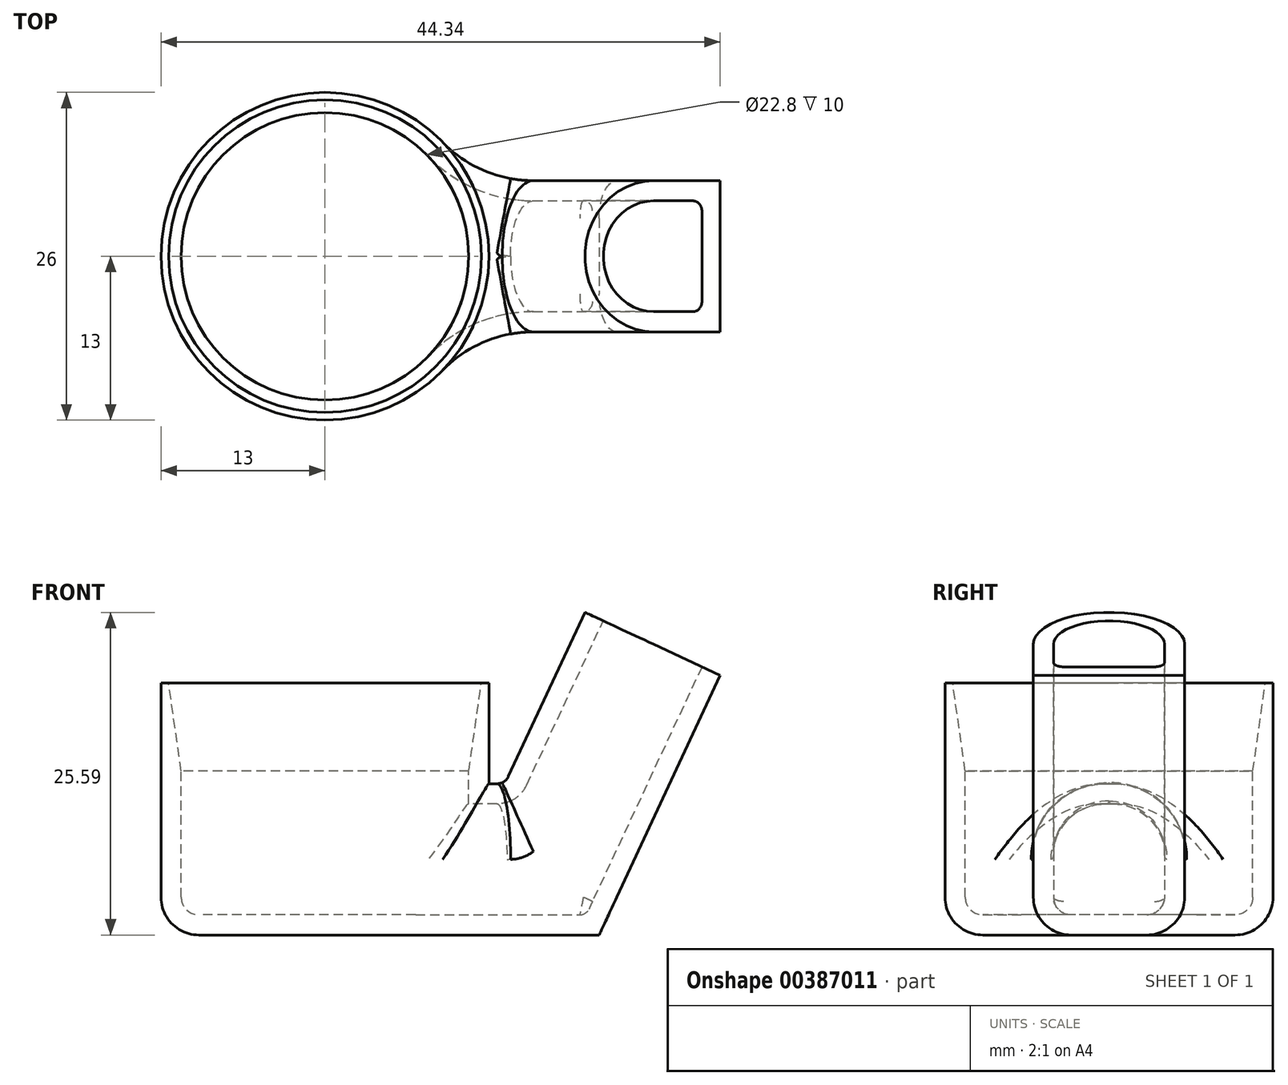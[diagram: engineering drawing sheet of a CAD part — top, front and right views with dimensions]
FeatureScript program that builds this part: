
annotation { "Feature Type Name" : "Feature", "Feature Type Description" : "" }
export const myFeature = defineFeature(function(context is Context, id is Id, definition is map)
    precondition{}
    {
        {
            var Q0;
            Q0=qCreatedBy(makeId("Top.planeOp"),FACE);
            var sketch = newSketch(context, id + "F0", { "sketchPlane" : qUnion([Q0])});
            skLineSegment(sketch, "E0.bottom", {"start": v(13, -13) * mm, "end": v(-13, -13) * mm});
            skLineSegment(sketch, "E0.top", {"start": v(13, 13) * mm, "end": v(-13, 13) * mm});
            skLineSegment(sketch, "E0.left", {"start": v(13, -13) * mm, "end": v(13, 13) * mm});
            skLineSegment(sketch, "E0.right", {"start": v(-13, -13) * mm, "end": v(-13, 13) * mm});
            skPoint(sketch, "E0.middle", {"position": v(0, 0) * mm});
            skSolve(sketch);
        }
        {
            var Q0;
            Q0 = qSketchRegion(id + "F0", true);
            extrude(context, id + "F1", {"entities" : qUnion([Q0]), "depth" : 20 * mm});
        }
        {
            var Q0;
            Q0=makeQuery(id+"F1.opExtrude","SWEPT_FACE",FACE,{"disambiguationData":[OSD([sQuery(id+"F0.wireOp",EDGE,"E0.left")])]});
            var sketch = newSketch(context, id + "F2", { "sketchPlane" : qUnion([Q0])});
            skLineSegment(sketch, "E1.bottom", {"start": v(6, 0) * mm, "end": v(-6, 0) * mm});
            skLineSegment(sketch, "E1.top", {"start": v(6, 12) * mm, "end": v(-6, 12) * mm});
            skLineSegment(sketch, "E1.left", {"start": v(6, 0) * mm, "end": v(6, 12) * mm});
            skLineSegment(sketch, "E1.right", {"start": v(-6, 0) * mm, "end": v(-6, 12) * mm});
            skSolve(sketch);
        }
        {
            var Q0;
            Q0 = qSketchRegion(id + "F2", true);
            extrude(context, id + "F3", {"entities" : qUnion([Q0]), "operationType" : NewBodyOperationType.ADD, "depth" : 12 * mm});
        }
        {
            var Q0;
            Q0=makeQuery(id+"F3.opExtrude","CAP_EDGE",EDGE,{"disambiguationData":[OSD([sQuery(id+"F2.wireOp",EDGE,"E1.top")])],"isStart":false});
            chamfer(context, id + "F4", {"entities" : qUnion([Q0]), "chamferType" : ChamferType.OFFSET_ANGLE, "width" : 5 * mm, "oppositeDirection" : false, "angle" : 65 * degree, "tangentPropagation" : true});
        }
        {
            var Q0;
            Q0=makeQuery(id+"F4.opChamfer","BLEND_FACE",FACE,{"disambiguationData":[OSD([sQuery(id+"F2.wireOp",EDGE,"E1.top")])]});
            extrude(context, id + "F5", {"entities" : qUnion([Q0]), "operationType" : NewBodyOperationType.ADD, "depth" : 15 * mm});
        }
        {
            var Q0;
            Q0=makeQuery(id+"F1.opExtrude","SWEPT_EDGE",EDGE,{"disambiguationData":[OSD([sQuery(id+"F0.wireOp",EDGE,"E0.top"),sQuery(id+"F0.wireOp",EDGE,"E0.right")])]});
            var Q1;
            Q1=makeQuery(id+"F1.opExtrude","SWEPT_EDGE",EDGE,{"disambiguationData":[OSD([sQuery(id+"F0.wireOp",EDGE,"E0.bottom"),sQuery(id+"F0.wireOp",EDGE,"E0.right")])]});
            var Q2;
            Q2=makeQuery(id+"F1.opExtrude","SWEPT_EDGE",EDGE,{"disambiguationData":[OSD([sQuery(id+"F0.wireOp",EDGE,"E0.top"),sQuery(id+"F0.wireOp",EDGE,"E0.left")])]});
            var Q3;
            Q3=makeQuery(id+"F1.opExtrude","SWEPT_EDGE",EDGE,{"disambiguationData":[OSD([sQuery(id+"F0.wireOp",EDGE,"E0.bottom"),sQuery(id+"F0.wireOp",EDGE,"E0.left")])]});
            fillet(context, id + "F6", {"entities" : qUnion([Q0, Q1, Q2, Q3]), "radius" : 13 * mm, "tangentPropagation" : true, "allowEdgeOverflow" : false});
        }
        {
            var Q0;
            Q0=makeQuery(id+"F5.opExtrude","SWEPT_FACE",FACE,{"disambiguationData":[OSD([sQuery(id+"F2.wireOp",EDGE,"E1.bottom"),sQuery(id+"F2.wireOp",EDGE,"E1.top"),sQuery(id+"F2.wireOp",EDGE,"E1.left"),sQuery(id+"F2.wireOp",EDGE,"E1.right")])]});
            var sketch = newSketch(context, id + "F7", { "sketchPlane" : qUnion([Q0])});
            skLineSegment(sketch, "E2.bottom", {"start": v(-6, 16.9) * mm, "end": v(6, 16.9) * mm});
            skLineSegment(sketch, "E2.top", {"start": v(-6, 20.23) * mm, "end": v(6, 20.23) * mm});
            skLineSegment(sketch, "E2.left", {"start": v(-6, 16.9) * mm, "end": v(-6, 20.23) * mm});
            skLineSegment(sketch, "E2.right", {"start": v(6, 16.9) * mm, "end": v(6, 20.23) * mm});
            skSolve(sketch);
        }
        {
            var Q0;
            Q0 = qSketchRegion(id + "F7", true);
            extrude(context, id + "F8", {"entities" : qUnion([Q0]), "operationType" : NewBodyOperationType.ADD, "depth" : 25 * mm, "offsetDistance" : 25 * mm});
        }
        {
            var Q0;
            Q0=makeQuery(id+"F8.opExtrude","SWEPT_FACE",FACE,{"disambiguationData":[OSD([sQuery(id+"F7.wireOp",EDGE,"E2.bottom")])]});
            extrude(context, id + "F9", {"entities" : qUnion([Q0]), "operationType" : NewBodyOperationType.REMOVE, "depth" : 25 * mm, "offsetDistance" : 25 * mm});
        }
        {
            var Q0;
            Q0=makeQuery(id+"F8.opExtrude","SWEPT_FACE",FACE,{"disambiguationData":[OSD([sQuery(id+"F7.wireOp",EDGE,"E2.bottom")])]});
            extrude(context, id + "F10", {"entities" : qUnion([Q0]), "operationType" : NewBodyOperationType.REMOVE, "oppositeDirection" : true, "depth" : 25 * mm, "offsetDistance" : 25 * mm});
        }
        {
            var Q0;
            {var subQ0=sQuery(id+"F2.wireOp",EDGE,"E1.right");Q0=makeQuery(id+"F6.opFillet","BLEND_EDGE",EDGE,{"blendedFrom":[makeQuery(id+"F1.opExtrude","SWEPT_EDGE",EDGE,{"disambiguationData":[OSD([sQuery(id+"F0.wireOp",EDGE,"E0.bottom"),sQuery(id+"F0.wireOp",EDGE,"E0.left")])]}),makeQuery(id+"F5.boolean.opBoolean","MERGE",FACE,{"derivedFrom":[makeQuery(id+"F3.opExtrude","SWEPT_FACE",FACE,{"disambiguationData":[OSD([subQ0])]}),makeQuery(id+"F5.opExtrude","SWEPT_FACE",FACE,{"disambiguationData":[OSD([sQuery(id+"F2.wireOp",EDGE,"E1.top"),subQ0])]})]})],"blendedInto":[makeQuery(id+"F5.boolean.opBoolean","MERGE",FACE,{"derivedFrom":[makeQuery(id+"F3.opExtrude","SWEPT_FACE",FACE,{"disambiguationData":[OSD([subQ0])]}),makeQuery(id+"F5.opExtrude","SWEPT_FACE",FACE,{"disambiguationData":[OSD([sQuery(id+"F2.wireOp",EDGE,"E1.top"),subQ0])]})]})]});}
            var Q1;
            {var subQ0=sQuery(id+"F2.wireOp",EDGE,"E1.left");Q1=makeQuery(id+"F6.opFillet","BLEND_EDGE",EDGE,{"blendedFrom":[makeQuery(id+"F1.opExtrude","SWEPT_EDGE",EDGE,{"disambiguationData":[OSD([sQuery(id+"F0.wireOp",EDGE,"E0.top"),sQuery(id+"F0.wireOp",EDGE,"E0.left")])]}),makeQuery(id+"F5.boolean.opBoolean","MERGE",FACE,{"derivedFrom":[makeQuery(id+"F3.opExtrude","SWEPT_FACE",FACE,{"disambiguationData":[OSD([subQ0])]}),makeQuery(id+"F5.opExtrude","SWEPT_FACE",FACE,{"disambiguationData":[OSD([sQuery(id+"F2.wireOp",EDGE,"E1.top"),subQ0])]})]})],"blendedInto":[makeQuery(id+"F5.boolean.opBoolean","MERGE",FACE,{"derivedFrom":[makeQuery(id+"F3.opExtrude","SWEPT_FACE",FACE,{"disambiguationData":[OSD([subQ0])]}),makeQuery(id+"F5.opExtrude","SWEPT_FACE",FACE,{"disambiguationData":[OSD([sQuery(id+"F2.wireOp",EDGE,"E1.top"),subQ0])]})]})]});}
            fillet(context, id + "F11", {"entities" : qUnion([Q0, Q1]), "radius" : 10 * mm, "tangentPropagation" : true, "allowEdgeOverflow" : false});
        }
        {
            var Q0;
            Q0=makeQuery(id+"F6.opFillet","BLEND_EDGE",EDGE,{"blendedFrom":[makeQuery(id+"F1.opExtrude","SWEPT_EDGE",EDGE,{"disambiguationData":[OSD([sQuery(id+"F0.wireOp",EDGE,"E0.top"),sQuery(id+"F0.wireOp",EDGE,"E0.left")])]}),makeQuery(id+"F3.opExtrude","SWEPT_FACE",FACE,{"disambiguationData":[OSD([sQuery(id+"F2.wireOp",EDGE,"E1.top")])]})],"blendedInto":[makeQuery(id+"F3.opExtrude","SWEPT_FACE",FACE,{"disambiguationData":[OSD([sQuery(id+"F2.wireOp",EDGE,"E1.top")])]})]});
            var Q1;
            {var subQ0=sQuery(id+"F2.wireOp",EDGE,"E1.top");Q1=makeQuery(id+"F5.boolean.opBoolean","MERGE",EDGE,{"derivedFrom":[makeQuery(id+"F4.opChamfer","BLEND_EDGE",EDGE,{"blendedFrom":[makeQuery(id+"F3.opExtrude","CAP_EDGE",EDGE,{"disambiguationData":[OSD([subQ0])],"isStart":false}),makeQuery(id+"F3.opExtrude","SWEPT_FACE",FACE,{"disambiguationData":[OSD([subQ0])]})],"blendedInto":[makeQuery(id+"F3.opExtrude","SWEPT_FACE",FACE,{"disambiguationData":[OSD([subQ0])]})]}),makeQuery(id+"F5.opExtrude","CAP_EDGE",EDGE,{"disambiguationData":[OSD([subQ0])],"isStart":true})]});}
            fillet(context, id + "F12", {"entities" : qUnion([Q0, Q1]), "radius" : 1 * mm, "tangentPropagation" : true, "allowEdgeOverflow" : false});
        }
        {
            var Q0;
            Q0=makeQuery(id+"F5.opExtrude","SWEPT_EDGE",EDGE,{"disambiguationData":[OSD([sQuery(id+"F2.wireOp",EDGE,"E1.top"),sQuery(id+"F2.wireOp",EDGE,"E1.left")])]});
            var Q1;
            {var subQ0=sQuery(id+"F7.wireOp",EDGE,"E2.right");var subQ1=sQuery(id+"F7.wireOp",EDGE,"E2.bottom");var subQ2=sQuery(id+"F2.wireOp",EDGE,"E1.right");var subQ3=sQuery(id+"F2.wireOp",EDGE,"E1.left");var subQ4=sQuery(id+"F2.wireOp",EDGE,"E1.top");var subQ5=sQuery(id+"F2.wireOp",EDGE,"E1.bottom");Q1=makeQuery(id+"F10.boolean.opBoolean","MERGE",EDGE,{"derivedFrom":[makeQuery(id+"F5.opExtrude","SWEPT_EDGE",EDGE,{"disambiguationData":[OSD([subQ5,subQ4,subQ3,subQ2]),TDD([makeQuery(id+"F4.opChamfer","BLEND_VERTEX",VERTEX,{"blendedFrom":[makeQuery(id+"F3.opExtrude","CAP_EDGE",EDGE,{"disambiguationData":[OSD([subQ4])],"isStart":false}),makeQuery(id+"F3.opExtrude","CAP_FACE",FACE,{"disambiguationData":[OSD([subQ5,subQ4,subQ3,subQ2])],"isStart":false}),makeQuery(id+"F3.opExtrude","SWEPT_FACE",FACE,{"disambiguationData":[OSD([subQ3])]})],"blendedInto":[makeQuery(id+"F3.opExtrude","CAP_FACE",FACE,{"disambiguationData":[OSD([subQ5,subQ4,subQ3,subQ2])],"isStart":false}),makeQuery(id+"F3.opExtrude","SWEPT_FACE",FACE,{"disambiguationData":[OSD([subQ3])]})]})])]}),makeQuery(id+"F9.boolean.opBoolean","COPY",EDGE,{"derivedFrom":makeQuery(id+"F9.opExtrude","SWEPT_EDGE",EDGE,{"disambiguationData":[OSD([subQ5,subQ4,subQ3,subQ2,subQ1,subQ0])]})}),makeQuery(id+"F10.opExtrude","SWEPT_EDGE",EDGE,{"disambiguationData":[OSD([subQ5,subQ4,subQ3,subQ2,subQ1,subQ0])]})]});}
            var Q2;
            Q2=makeQuery(id+"F5.opExtrude","SWEPT_EDGE",EDGE,{"disambiguationData":[OSD([sQuery(id+"F2.wireOp",EDGE,"E1.top"),sQuery(id+"F2.wireOp",EDGE,"E1.right")])]});
            var Q3;
            {var subQ0=sQuery(id+"F7.wireOp",EDGE,"E2.left");var subQ1=sQuery(id+"F7.wireOp",EDGE,"E2.bottom");var subQ2=sQuery(id+"F2.wireOp",EDGE,"E1.right");var subQ3=sQuery(id+"F2.wireOp",EDGE,"E1.left");var subQ4=sQuery(id+"F2.wireOp",EDGE,"E1.top");var subQ5=sQuery(id+"F2.wireOp",EDGE,"E1.bottom");Q3=makeQuery(id+"F10.boolean.opBoolean","MERGE",EDGE,{"derivedFrom":[makeQuery(id+"F5.opExtrude","SWEPT_EDGE",EDGE,{"disambiguationData":[OSD([subQ5,subQ4,subQ3,subQ2]),TDD([makeQuery(id+"F4.opChamfer","BLEND_VERTEX",VERTEX,{"blendedFrom":[makeQuery(id+"F3.opExtrude","CAP_EDGE",EDGE,{"disambiguationData":[OSD([subQ4])],"isStart":false}),makeQuery(id+"F3.opExtrude","CAP_FACE",FACE,{"disambiguationData":[OSD([subQ5,subQ4,subQ3,subQ2])],"isStart":false}),makeQuery(id+"F3.opExtrude","SWEPT_FACE",FACE,{"disambiguationData":[OSD([subQ2])]})],"blendedInto":[makeQuery(id+"F3.opExtrude","CAP_FACE",FACE,{"disambiguationData":[OSD([subQ5,subQ4,subQ3,subQ2])],"isStart":false}),makeQuery(id+"F3.opExtrude","SWEPT_FACE",FACE,{"disambiguationData":[OSD([subQ2])]})]})])]}),makeQuery(id+"F9.boolean.opBoolean","COPY",EDGE,{"derivedFrom":makeQuery(id+"F9.opExtrude","SWEPT_EDGE",EDGE,{"disambiguationData":[OSD([subQ5,subQ4,subQ3,subQ2,subQ1,subQ0])]})}),makeQuery(id+"F10.opExtrude","SWEPT_EDGE",EDGE,{"disambiguationData":[OSD([subQ5,subQ4,subQ3,subQ2,subQ1,subQ0])]})]});}
            fillet(context, id + "F13", {"entities" : qUnion([Q0, Q1, Q2, Q3]), "radius" : 6 * mm, "tangentPropagation" : true, "allowEdgeOverflow" : false});
        }
        {
            var Q0;
            {var subQ0=sQuery(id+"F0.wireOp",EDGE,"E0.left");var subQ1=sQuery(id+"F0.wireOp",EDGE,"E0.bottom");Q0=makeQuery(id+"F6.opFillet","BLEND_EDGE",EDGE,{"blendedFrom":[makeQuery(id+"F1.opExtrude","SWEPT_EDGE",EDGE,{"disambiguationData":[OSD([subQ1,subQ0])]}),makeQuery(id+"F3.boolean.opBoolean","MERGE",FACE,{"derivedFrom":[makeQuery(id+"F1.opExtrude","CAP_FACE",FACE,{"disambiguationData":[OSD([subQ1,sQuery(id+"F0.wireOp",EDGE,"E0.top"),subQ0,sQuery(id+"F0.wireOp",EDGE,"E0.right")])],"isStart":true}),makeQuery(id+"F3.opExtrude","SWEPT_FACE",FACE,{"disambiguationData":[OSD([sQuery(id+"F2.wireOp",EDGE,"E1.bottom")])]})]})],"blendedInto":[makeQuery(id+"F3.boolean.opBoolean","MERGE",FACE,{"derivedFrom":[makeQuery(id+"F1.opExtrude","CAP_FACE",FACE,{"disambiguationData":[OSD([subQ1,sQuery(id+"F0.wireOp",EDGE,"E0.top"),subQ0,sQuery(id+"F0.wireOp",EDGE,"E0.right")])],"isStart":true}),makeQuery(id+"F3.opExtrude","SWEPT_FACE",FACE,{"disambiguationData":[OSD([sQuery(id+"F2.wireOp",EDGE,"E1.bottom")])]})]})]});}
            fillet(context, id + "F14", {"entities" : qUnion([Q0]), "radius" : 3 * mm, "tangentPropagation" : true, "allowEdgeOverflow" : false});
        }
        {
            var Q0;
            Q0=makeQuery(id+"F1.opExtrude","CAP_FACE",FACE,{"disambiguationData":[OSD([sQuery(id+"F0.wireOp",EDGE,"E0.bottom"),sQuery(id+"F0.wireOp",EDGE,"E0.top"),sQuery(id+"F0.wireOp",EDGE,"E0.left"),sQuery(id+"F0.wireOp",EDGE,"E0.right")])],"isStart":false});
            var Q1;
            Q1=makeQuery(id+"F5.opExtrude","CAP_FACE",FACE,{"disambiguationData":[OSD([sQuery(id+"F2.wireOp",EDGE,"E1.top")])],"isStart":false});
            shell(context, id + "F15", {"entities" : qUnion([Q0, Q1]), "thickness" : 1.6 * mm});
        }
        {
            var Q0;
            {var subQ0=sQuery(id+"F2.wireOp",EDGE,"E1.top");var subQ1=sQuery(id+"F7.wireOp",EDGE,"E2.right");var subQ2=sQuery(id+"F7.wireOp",EDGE,"E2.bottom");var subQ3=sQuery(id+"F2.wireOp",EDGE,"E1.right");var subQ4=sQuery(id+"F2.wireOp",EDGE,"E1.left");var subQ5=sQuery(id+"F2.wireOp",EDGE,"E1.bottom");Q0=makeQuery(id+"F15.opShell","OFFSET_EDGE",EDGE,{"disambiguationData":[OSD([subQ5,subQ0,subQ4,subQ3,subQ2,subQ1]),TDD([makeQuery(id+"F13.opFillet","BLEND_EDGE",EDGE,{"blendedFrom":[makeQuery(id+"F10.boolean.opBoolean","MERGE",EDGE,{"derivedFrom":[makeQuery(id+"F5.opExtrude","SWEPT_EDGE",EDGE,{"disambiguationData":[OSD([subQ5,subQ0,subQ4,subQ3]),TDD([makeQuery(id+"F4.opChamfer","BLEND_VERTEX",VERTEX,{"blendedFrom":[makeQuery(id+"F3.opExtrude","CAP_EDGE",EDGE,{"disambiguationData":[OSD([subQ0])],"isStart":false}),makeQuery(id+"F3.opExtrude","CAP_FACE",FACE,{"disambiguationData":[OSD([subQ5,subQ0,subQ4,subQ3])],"isStart":false}),makeQuery(id+"F3.opExtrude","SWEPT_FACE",FACE,{"disambiguationData":[OSD([subQ4])]})],"blendedInto":[makeQuery(id+"F3.opExtrude","CAP_FACE",FACE,{"disambiguationData":[OSD([subQ5,subQ0,subQ4,subQ3])],"isStart":false}),makeQuery(id+"F3.opExtrude","SWEPT_FACE",FACE,{"disambiguationData":[OSD([subQ4])]})]})])]}),makeQuery(id+"F9.boolean.opBoolean","COPY",EDGE,{"derivedFrom":makeQuery(id+"F9.opExtrude","SWEPT_EDGE",EDGE,{"disambiguationData":[OSD([subQ5,subQ0,subQ4,subQ3,subQ2,subQ1])]})}),makeQuery(id+"F10.opExtrude","SWEPT_EDGE",EDGE,{"disambiguationData":[OSD([subQ5,subQ0,subQ4,subQ3,subQ2,subQ1])]})]}),makeQuery(id+"F5.opExtrude","CAP_FACE",FACE,{"disambiguationData":[OSD([subQ0])],"isStart":false})],"blendedInto":[makeQuery(id+"F5.opExtrude","CAP_FACE",FACE,{"disambiguationData":[OSD([subQ0])],"isStart":false})]})])]});}
            var Q1;
            {var subQ0=sQuery(id+"F2.wireOp",EDGE,"E1.top");Q1=makeQuery(id+"F13.opFillet","BLEND_EDGE",EDGE,{"blendedFrom":[makeQuery(id+"F5.opExtrude","SWEPT_EDGE",EDGE,{"disambiguationData":[OSD([subQ0,sQuery(id+"F2.wireOp",EDGE,"E1.right")])]}),makeQuery(id+"F5.opExtrude","CAP_FACE",FACE,{"disambiguationData":[OSD([subQ0])],"isStart":false})],"blendedInto":[makeQuery(id+"F5.opExtrude","CAP_FACE",FACE,{"disambiguationData":[OSD([subQ0])],"isStart":false})]});}
            fillet(context, id + "F16", {"entities" : qUnion([Q0, Q1]), "radius" : 0.8 * mm, "tangentPropagation" : true, "allowEdgeOverflow" : false});
        }
        {
            var Q0;
            Q0=makeQuery(id+"F15.opShell","OFFSET_EDGE",EDGE,{"disambiguationData":[OSD([sQuery(id+"F0.wireOp",EDGE,"E0.bottom"),sQuery(id+"F0.wireOp",EDGE,"E0.top"),sQuery(id+"F0.wireOp",EDGE,"E0.left"),sQuery(id+"F0.wireOp",EDGE,"E0.right")])]});
            chamfer(context, id + "F17", {"entities" : qUnion([Q0]), "chamferType" : ChamferType.TWO_OFFSETS, "width1" : 7 * mm, "oppositeDirection" : false, "width2" : 1 * mm, "tangentPropagation" : true});
        }
    });
